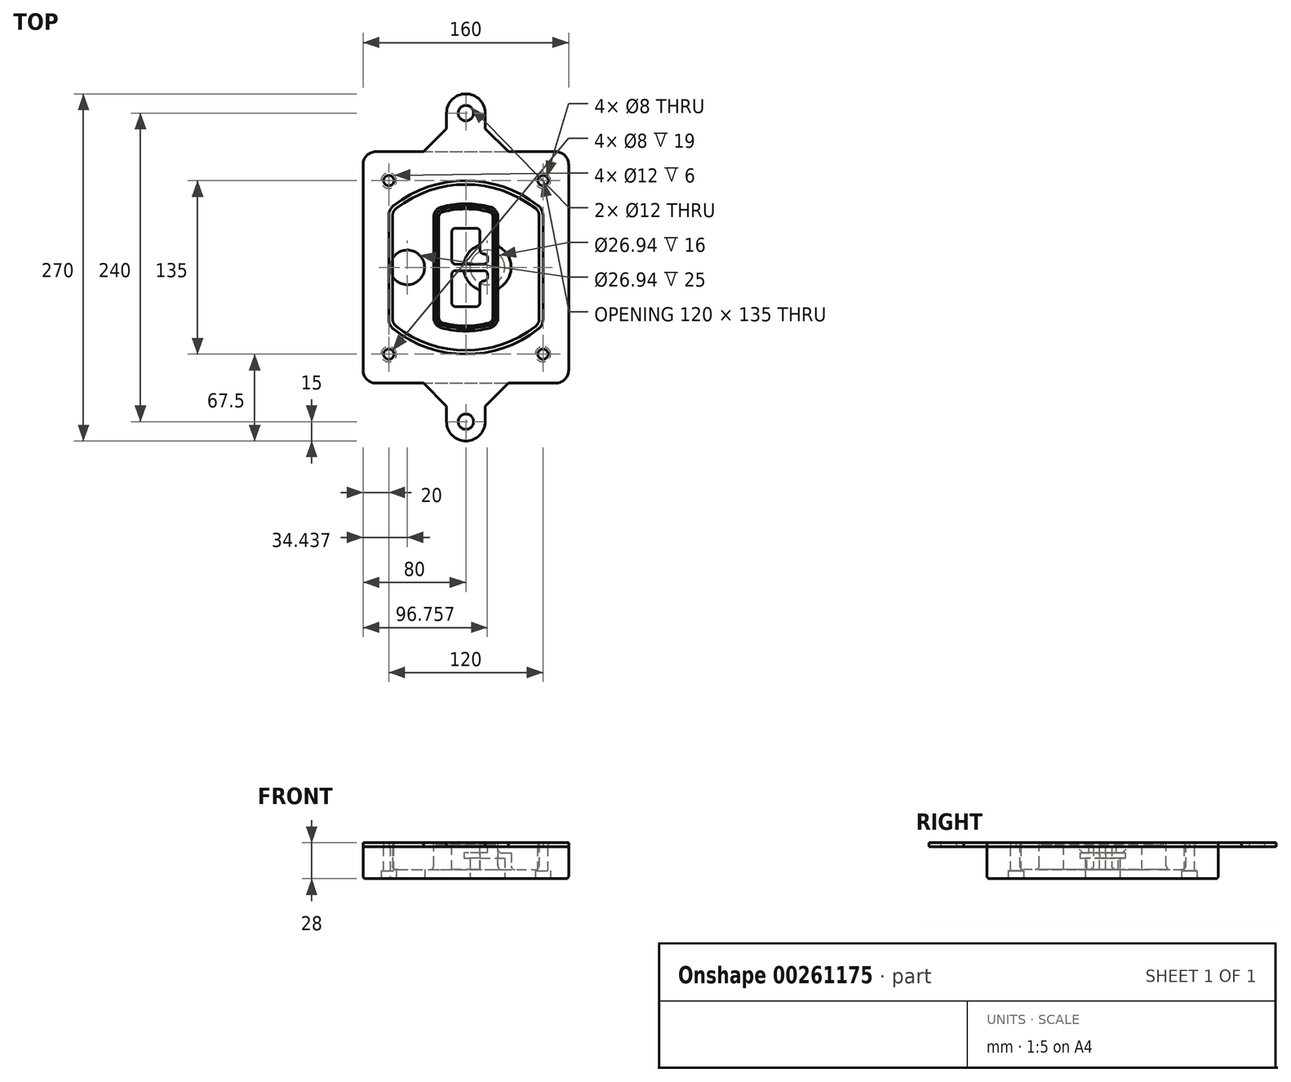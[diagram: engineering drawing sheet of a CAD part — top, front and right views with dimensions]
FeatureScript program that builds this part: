
annotation { "Feature Type Name" : "Feature", "Feature Type Description" : "" }
export const myFeature = defineFeature(function(context is Context, id is Id, definition is map)
    precondition{}
    {
        {
            var Q0;
            Q0=qCreatedBy(makeId("Top.planeOp"),FACE);
            var sketch = newSketch(context, id + "F0", { "sketchPlane" : qUnion([Q0])});
            skPoint(sketch, "E0.rect.middle", {"position": v(0, 0) * mm});
            skLineSegment(sketch, "E1.bottom", {"start": v(-70, -90) * mm, "end": v(70, -90) * mm});
            skLineSegment(sketch, "E1.top", {"start": v(-70, 90) * mm, "end": v(70, 90) * mm});
            skLineSegment(sketch, "E1.left", {"start": v(-80, -80) * mm, "end": v(-80, 80) * mm});
            skLineSegment(sketch, "E1.right", {"start": v(80, -80) * mm, "end": v(80, 80) * mm});
            skLineSegment(sketch, "E2", {"start": v(-80, 90) * mm, "end": v(80, -90) * mm, "construction": true});
            skLineSegment(sketch, "E3", {"start": v(80, 90) * mm, "end": v(-80, -90) * mm, "construction": true});
            skCircle(sketch, "E4", {"center": v(-60, 67.5) * mm, "radius": 4 * mm});
            skCircle(sketch, "E5", {"center": v(60, 67.5) * mm, "radius": 4 * mm});
            skCircle(sketch, "E6", {"center": v(60, -67.5) * mm, "radius": 4 * mm});
            skCircle(sketch, "E7", {"center": v(-60, -67.5) * mm, "radius": 4 * mm});
            skLineSegment(sketch, "E8", {"start": v(-60, 67.5) * mm, "end": v(60, 67.5) * mm, "construction": true});
            skLineSegment(sketch, "E9", {"start": v(60, 67.5) * mm, "end": v(60, -67.5) * mm, "construction": true});
            skLineSegment(sketch, "E10", {"start": v(60, -67.5) * mm, "end": v(-60, -67.5) * mm, "construction": true});
            skLineSegment(sketch, "E11", {"start": v(-60, -67.5) * mm, "end": v(-60, 67.5) * mm, "construction": true});
            skLineSegment(sketch, "E12", {"start": v(-60, 40.3) * mm, "end": v(-60, -40.3) * mm});
            skLineSegment(sketch, "E13", {"start": v(60, 40.3) * mm, "end": v(60, -40.3) * mm});
            skArc(sketch, "E14", {"start": v(56.15, 48.18) * mm, "mid": v(0, 67.5) * mm, "end": v(-56.15, 48.18) * mm});
            skArc(sketch, "E15", {"start": v(-56.15, -48.18) * mm, "mid": v(0, -67.5) * mm, "end": v(56.15, -48.18) * mm});
            skLineSegment(sketch, "E16", {"start": v(-60, 0) * mm, "end": v(60, 0) * mm, "construction": true});
            skPoint(sketch, "E17.visualSharp", {"position": v(-60, -45) * mm});
            skArc(sketch, "E17.filletArc", {"start": v(-60, -40.3) * mm, "mid": v(-58.99, -44.68) * mm, "end": v(-56.15, -48.18) * mm});
            skPoint(sketch, "E18.visualSharp", {"position": v(-60, 45) * mm});
            skArc(sketch, "E18.filletArc", {"start": v(-56.15, 48.18) * mm, "mid": v(-58.99, 44.68) * mm, "end": v(-60, 40.3) * mm});
            skPoint(sketch, "E19.visualSharp", {"position": v(60, 45) * mm});
            skArc(sketch, "E19.filletArc", {"start": v(60, 40.3) * mm, "mid": v(58.99, 44.68) * mm, "end": v(56.15, 48.18) * mm});
            skPoint(sketch, "E20.visualSharp", {"position": v(60, -45) * mm});
            skArc(sketch, "E20.filletArc", {"start": v(56.15, -48.18) * mm, "mid": v(58.99, -44.68) * mm, "end": v(60, -40.3) * mm});
            skPoint(sketch, "E21.visualSharp", {"position": v(-80, 90) * mm});
            skArc(sketch, "E21.filletArc", {"start": v(-70, 90) * mm, "mid": v(-77.07, 87.07) * mm, "end": v(-80, 80) * mm});
            skPoint(sketch, "E22.visualSharp", {"position": v(80, 90) * mm});
            skArc(sketch, "E22.filletArc", {"start": v(80, 80) * mm, "mid": v(77.07, 87.07) * mm, "end": v(70, 90) * mm});
            skPoint(sketch, "E23.visualSharp", {"position": v(80, -90) * mm});
            skArc(sketch, "E23.filletArc", {"start": v(70, -90) * mm, "mid": v(77.07, -87.07) * mm, "end": v(80, -80) * mm});
            skPoint(sketch, "E24.visualSharp", {"position": v(-80, -90) * mm});
            skArc(sketch, "E24.filletArc", {"start": v(-80, -80) * mm, "mid": v(-77.07, -87.07) * mm, "end": v(-70, -90) * mm});
            skArc(sketch, "E25.0", {"start": v(57, 40.3) * mm, "mid": v(56.3, 43.36) * mm, "end": v(54.3, 45.81) * mm});
            skLineSegment(sketch, "E25.1", {"start": v(57, 40.3) * mm, "end": v(57, -40.3) * mm});
            skArc(sketch, "E25.2", {"start": v(54.3, -45.81) * mm, "mid": v(56.3, -43.36) * mm, "end": v(57, -40.3) * mm});
            skArc(sketch, "E25.3", {"start": v(-54.3, -45.81) * mm, "mid": v(0, -64.5) * mm, "end": v(54.3, -45.81) * mm});
            skArc(sketch, "E25.4", {"start": v(-57, -40.3) * mm, "mid": v(-56.3, -43.36) * mm, "end": v(-54.3, -45.81) * mm});
            skArc(sketch, "E25.5", {"start": v(54.3, 45.81) * mm, "mid": v(0, 64.5) * mm, "end": v(-54.3, 45.81) * mm});
            skLineSegment(sketch, "E25.6", {"start": v(-57, 40.3) * mm, "end": v(-57, -40.3) * mm});
            skArc(sketch, "E25.7", {"start": v(-54.3, 45.81) * mm, "mid": v(-56.3, 43.36) * mm, "end": v(-57, 40.3) * mm});
            skArc(sketch, "E26.0", {"start": v(-58.62, 51.33) * mm, "mid": v(-62.58, 46.43) * mm, "end": v(-64, 40.3) * mm});
            skArc(sketch, "E26.1", {"start": v(58.62, 51.33) * mm, "mid": v(0, 71.5) * mm, "end": v(-58.62, 51.33) * mm});
            skArc(sketch, "E26.2", {"start": v(64, 40.3) * mm, "mid": v(62.58, 46.43) * mm, "end": v(58.62, 51.33) * mm});
            skLineSegment(sketch, "E26.3", {"start": v(64, 40.3) * mm, "end": v(64, -40.3) * mm});
            skArc(sketch, "E26.4", {"start": v(58.62, -51.33) * mm, "mid": v(62.58, -46.43) * mm, "end": v(64, -40.3) * mm});
            skLineSegment(sketch, "E26.5", {"start": v(-64, 40.3) * mm, "end": v(-64, -40.3) * mm});
            skArc(sketch, "E26.6", {"start": v(-58.62, -51.33) * mm, "mid": v(0, -71.5) * mm, "end": v(58.62, -51.33) * mm});
            skArc(sketch, "E26.7", {"start": v(-64, -40.3) * mm, "mid": v(-62.58, -46.43) * mm, "end": v(-58.62, -51.33) * mm});
            skSolve(sketch);
        }
        {
            var Q0;
            Q0=makeQuery(id+"F0.imprint","IMPRINT",FACE,{"disambiguationData":[TD([[makeQuery(id+"F0.imprint","IMPRINT",EDGE,{"derivedFrom":sQuery(id+"F0.wireOp",EDGE,"E1.bottom")}),1.0]])]});
            var Q1;
            Q1=makeQuery(id+"F0.imprint","IMPRINT",FACE,{"disambiguationData":[TD([[makeQuery(id+"F0.imprint","IMPRINT",EDGE,{"derivedFrom":sQuery(id+"F0.wireOp",EDGE,"E12")}),1.0]])]});
            var Q2;
            Q2=makeQuery(id+"F0.imprint","IMPRINT",FACE,{"disambiguationData":[TD([[makeQuery(id+"F0.imprint","IMPRINT",EDGE,{"derivedFrom":sQuery(id+"F0.wireOp",EDGE,"E25.0")}),1.0]])]});
            var Q3;
            Q3=makeQuery(id+"F0.imprint","IMPRINT",FACE,{"disambiguationData":[TD([[makeQuery(id+"F0.imprint","IMPRINT",EDGE,{"derivedFrom":sQuery(id+"F0.wireOp",EDGE,"E12")}),-1.0]])]});
            extrude(context, id + "F1", {"entities" : qUnion([Q0, Q1, Q2, Q3]), "oppositeDirection" : true, "depth" : 25 * mm});
        }
        {
            var Q0;
            Q0=makeQuery(id+"F0.imprint","IMPRINT",FACE,{"disambiguationData":[TD([[makeQuery(id+"F0.imprint","IMPRINT",EDGE,{"derivedFrom":sQuery(id+"F0.wireOp",EDGE,"E12")}),1.0]])]});
            extrude(context, id + "F2", {"entities" : qUnion([Q0]), "operationType" : NewBodyOperationType.ADD, "depth" : 3 * mm});
        }
        {
            var Q0;
            Q0=makeQuery(id+"F0.imprint","IMPRINT",FACE,{"disambiguationData":[TD([[makeQuery(id+"F0.imprint","IMPRINT",EDGE,{"derivedFrom":sQuery(id+"F0.wireOp",EDGE,"E25.0")}),1.0]])]});
            extrude(context, id + "F3", {"entities" : qUnion([Q0]), "operationType" : NewBodyOperationType.REMOVE, "oppositeDirection" : true, "depth" : 18 * mm});
        }
        {
            var Q0;
            Q0=makeQuery(id+"F2.opExtrude","CAP_FACE",FACE,{"disambiguationData":[OSD([sQuery(id+"F0.wireOp",EDGE,"E12"),sQuery(id+"F0.wireOp",EDGE,"E13"),sQuery(id+"F0.wireOp",EDGE,"E14"),sQuery(id+"F0.wireOp",EDGE,"E15"),sQuery(id+"F0.wireOp",EDGE,"E17.filletArc"),sQuery(id+"F0.wireOp",EDGE,"E18.filletArc"),sQuery(id+"F0.wireOp",EDGE,"E19.filletArc"),sQuery(id+"F0.wireOp",EDGE,"E20.filletArc"),sQuery(id+"F0.wireOp",EDGE,"E25.0"),sQuery(id+"F0.wireOp",EDGE,"E25.1"),sQuery(id+"F0.wireOp",EDGE,"E25.2"),sQuery(id+"F0.wireOp",EDGE,"E25.3"),sQuery(id+"F0.wireOp",EDGE,"E25.4"),sQuery(id+"F0.wireOp",EDGE,"E25.5"),sQuery(id+"F0.wireOp",EDGE,"E25.6"),sQuery(id+"F0.wireOp",EDGE,"E25.7")])],"isStart":false});
            var sketch = newSketch(context, id + "F4", { "sketchPlane" : qUnion([Q0])});
            skArc(sketch, "E27.0", {"start": v(-19.08, -46.97) * mm, "mid": v(0, -49.5) * mm, "end": v(19.08, -46.97) * mm});
            skArc(sketch, "E28.0", {"start": v(19.08, 46.97) * mm, "mid": v(0, 49.5) * mm, "end": v(-19.08, 46.97) * mm});
            skLineSegment(sketch, "E29", {"start": v(-25, 39.25) * mm, "end": v(-25, -39.25) * mm});
            skLineSegment(sketch, "E30", {"start": v(25, 39.25) * mm, "end": v(25, -39.25) * mm});
            skLineSegment(sketch, "E31", {"start": v(-25, 45.1) * mm, "end": v(25, 45.1) * mm, "construction": true});
            skLineSegment(sketch, "E32", {"start": v(-25, -45.1) * mm, "end": v(25, -45.1) * mm, "construction": true});
            skPoint(sketch, "E33.visualSharp", {"position": v(-25, 45.1) * mm});
            skArc(sketch, "E33.filletArc", {"start": v(-19.08, 46.97) * mm, "mid": v(-23.35, 44.11) * mm, "end": v(-25, 39.25) * mm});
            skPoint(sketch, "E34.visualSharp", {"position": v(25, 45.1) * mm});
            skArc(sketch, "E34.filletArc", {"start": v(25, 39.25) * mm, "mid": v(23.35, 44.11) * mm, "end": v(19.08, 46.97) * mm});
            skPoint(sketch, "E35.visualSharp", {"position": v(25, -45.1) * mm});
            skArc(sketch, "E35.filletArc", {"start": v(19.08, -46.97) * mm, "mid": v(23.35, -44.11) * mm, "end": v(25, -39.25) * mm});
            skPoint(sketch, "E36.visualSharp", {"position": v(-25, -45.1) * mm});
            skArc(sketch, "E36.filletArc", {"start": v(-25, -39.25) * mm, "mid": v(-23.35, -44.11) * mm, "end": v(-19.08, -46.97) * mm});
            skArc(sketch, "E37.0", {"start": v(54.3, 45.81) * mm, "mid": v(0, 64.5) * mm, "end": v(-54.3, 45.81) * mm});
            skArc(sketch, "E37.1", {"start": v(-54.3, 45.81) * mm, "mid": v(-56.3, 43.36) * mm, "end": v(-57, 40.3) * mm});
            skLineSegment(sketch, "E37.2", {"start": v(-57, 40.3) * mm, "end": v(-57, -40.3) * mm});
            skArc(sketch, "E37.3", {"start": v(-57, -40.3) * mm, "mid": v(-56.3, -43.36) * mm, "end": v(-54.3, -45.81) * mm});
            skArc(sketch, "E37.4", {"start": v(-54.3, -45.81) * mm, "mid": v(0, -64.5) * mm, "end": v(54.3, -45.81) * mm});
            skArc(sketch, "E37.5", {"start": v(54.3, -45.81) * mm, "mid": v(56.3, -43.36) * mm, "end": v(57, -40.3) * mm});
            skLineSegment(sketch, "E37.6", {"start": v(57, 40.3) * mm, "end": v(57, -40.3) * mm});
            skArc(sketch, "E37.7", {"start": v(57, 40.3) * mm, "mid": v(56.3, 43.36) * mm, "end": v(54.3, 45.81) * mm});
            skLineSegment(sketch, "E38.0", {"start": v(23, 39.25) * mm, "end": v(23, -39.25) * mm});
            skArc(sketch, "E38.1", {"start": v(18.56, -45.04) * mm, "mid": v(21.76, -42.9) * mm, "end": v(23, -39.25) * mm});
            skArc(sketch, "E38.2", {"start": v(-18.56, -45.04) * mm, "mid": v(0, -47.5) * mm, "end": v(18.56, -45.04) * mm});
            skArc(sketch, "E38.3", {"start": v(-23, -39.25) * mm, "mid": v(-21.76, -42.9) * mm, "end": v(-18.56, -45.04) * mm});
            skLineSegment(sketch, "E38.4", {"start": v(-23, 39.25) * mm, "end": v(-23, -39.25) * mm});
            skArc(sketch, "E38.5", {"start": v(23, 39.25) * mm, "mid": v(21.76, 42.9) * mm, "end": v(18.56, 45.04) * mm});
            skArc(sketch, "E38.6", {"start": v(-18.56, 45.04) * mm, "mid": v(-21.76, 42.9) * mm, "end": v(-23, 39.25) * mm});
            skArc(sketch, "E38.7", {"start": v(18.56, 45.04) * mm, "mid": v(0, 47.5) * mm, "end": v(-18.56, 45.04) * mm});
            skArc(sketch, "E39.0", {"start": v(21, 39.25) * mm, "mid": v(20.18, 41.68) * mm, "end": v(18.04, 43.1) * mm});
            skLineSegment(sketch, "E39.1", {"start": v(21, 39.25) * mm, "end": v(21, -39.25) * mm});
            skArc(sketch, "E39.2", {"start": v(18.04, -43.1) * mm, "mid": v(20.18, -41.68) * mm, "end": v(21, -39.25) * mm});
            skArc(sketch, "E39.3", {"start": v(-18.04, -43.1) * mm, "mid": v(0, -45.5) * mm, "end": v(18.04, -43.1) * mm});
            skArc(sketch, "E39.4", {"start": v(-21, -39.25) * mm, "mid": v(-20.18, -41.68) * mm, "end": v(-18.04, -43.1) * mm});
            skArc(sketch, "E39.5", {"start": v(18.04, 43.1) * mm, "mid": v(0, 45.5) * mm, "end": v(-18.04, 43.1) * mm});
            skLineSegment(sketch, "E39.6", {"start": v(-21, 39.25) * mm, "end": v(-21, -39.25) * mm});
            skArc(sketch, "E39.7", {"start": v(-18.04, 43.1) * mm, "mid": v(-20.18, 41.68) * mm, "end": v(-21, 39.25) * mm});
            skLineSegment(sketch, "E40", {"start": v(-25, 0) * mm, "end": v(25, 0) * mm, "construction": true});
            skLineSegment(sketch, "E41", {"start": v(-11, 5.5) * mm, "end": v(-11, 27.5) * mm});
            skLineSegment(sketch, "E42", {"start": v(-8, 30.5) * mm, "end": v(8, 30.5) * mm});
            skLineSegment(sketch, "E43", {"start": v(11, 27.5) * mm, "end": v(11, 13.5) * mm});
            skLineSegment(sketch, "E44", {"start": v(14, 10.5) * mm, "end": v(14, 10.5) * mm});
            skLineSegment(sketch, "E45", {"start": v(17, 7.5) * mm, "end": v(17, 5.5) * mm});
            skLineSegment(sketch, "E46", {"start": v(14, 2.5) * mm, "end": v(-8, 2.5) * mm});
            skPoint(sketch, "E47.visualSharp", {"position": v(-11, 30.5) * mm});
            skArc(sketch, "E47.filletArc", {"start": v(-8, 30.5) * mm, "mid": v(-10.12, 29.62) * mm, "end": v(-11, 27.5) * mm});
            skPoint(sketch, "E48.visualSharp", {"position": v(11, 30.5) * mm});
            skArc(sketch, "E48.filletArc", {"start": v(11, 27.5) * mm, "mid": v(10.12, 29.62) * mm, "end": v(8, 30.5) * mm});
            skPoint(sketch, "E49.visualSharp", {"position": v(11, 10.5) * mm});
            skArc(sketch, "E49.filletArc", {"start": v(11, 13.5) * mm, "mid": v(11.88, 11.38) * mm, "end": v(14, 10.5) * mm});
            skPoint(sketch, "E50.visualSharp", {"position": v(17, 10.5) * mm});
            skArc(sketch, "E50.filletArc", {"start": v(17, 7.5) * mm, "mid": v(16.12, 9.62) * mm, "end": v(14, 10.5) * mm});
            skPoint(sketch, "E51.visualSharp", {"position": v(17, 2.5) * mm});
            skArc(sketch, "E51.filletArc", {"start": v(14, 2.5) * mm, "mid": v(16.12, 3.38) * mm, "end": v(17, 5.5) * mm});
            skPoint(sketch, "E52.visualSharp", {"position": v(-11, 2.5) * mm});
            skArc(sketch, "E52.filletArc", {"start": v(-11, 5.5) * mm, "mid": v(-10.12, 3.38) * mm, "end": v(-8, 2.5) * mm});
            skLineSegment(sketch, "E53.0.MirrorCS", {"start": v(14, -2.5) * mm, "end": v(-8, -2.5) * mm});
            skArc(sketch, "E54.0.MirrorCS", {"start": v(-11, -5.5) * mm, "mid": v(-10.12, -3.38) * mm, "end": v(-8, -2.5) * mm});
            skLineSegment(sketch, "E55.0.MirrorCS", {"start": v(-11, -5.5) * mm, "end": v(-11, -27.5) * mm});
            skArc(sketch, "E56.0.MirrorCS", {"start": v(-8, -30.5) * mm, "mid": v(-10.12, -29.62) * mm, "end": v(-11, -27.5) * mm});
            skLineSegment(sketch, "E57.0.MirrorCS", {"start": v(-8, -30.5) * mm, "end": v(8, -30.5) * mm});
            skArc(sketch, "E58.0.MirrorCS", {"start": v(11, -27.5) * mm, "mid": v(10.12, -29.62) * mm, "end": v(8, -30.5) * mm});
            skLineSegment(sketch, "E59.0.MirrorCS", {"start": v(11, -27.5) * mm, "end": v(11, -13.5) * mm});
            skArc(sketch, "E60.0.MirrorCS", {"start": v(11, -13.5) * mm, "mid": v(11.88, -11.38) * mm, "end": v(14, -10.5) * mm});
            skArc(sketch, "E61.0.MirrorCS", {"start": v(17, -7.5) * mm, "mid": v(16.12, -9.62) * mm, "end": v(14, -10.5) * mm});
            skLineSegment(sketch, "E62.0.MirrorCS", {"start": v(17, -7.5) * mm, "end": v(17, -5.5) * mm});
            skArc(sketch, "E63.0.MirrorCS", {"start": v(14, -2.5) * mm, "mid": v(16.12, -3.38) * mm, "end": v(17, -5.5) * mm});
            skSolve(sketch);
        }
        {
            var Q0;
            Q0=makeQuery(id+"F4.imprint","IMPRINT",FACE,{"disambiguationData":[TD([[makeQuery(id+"F4.imprint","IMPRINT",EDGE,{"derivedFrom":sQuery(id+"F4.wireOp",EDGE,"E27.0")}),1.0]])]});
            var Q1;
            Q1=makeQuery(id+"F4.imprint","IMPRINT",FACE,{"disambiguationData":[TD([[makeQuery(id+"F4.imprint","IMPRINT",EDGE,{"derivedFrom":sQuery(id+"F4.wireOp",EDGE,"E38.0")}),-1.0]])]});
            var Q2;
            Q2=makeQuery(id+"F4.imprint","IMPRINT",FACE,{"disambiguationData":[TD([[makeQuery(id+"F4.imprint","IMPRINT",EDGE,{"derivedFrom":sQuery(id+"F4.wireOp",EDGE,"E39.0")}),1.0]])]});
            extrude(context, id + "F5", {"entities" : qUnion([Q0, Q1, Q2]), "operationType" : NewBodyOperationType.ADD, "endBound" : BoundingType.UP_TO_NEXT, "oppositeDirection" : true, "depth" : 25 * mm});
        }
        {
            var Q0;
            Q0=makeQuery(id+"F4.imprint","IMPRINT",FACE,{"disambiguationData":[TD([[makeQuery(id+"F4.imprint","IMPRINT",EDGE,{"derivedFrom":sQuery(id+"F4.wireOp",EDGE,"E38.0")}),-1.0]])]});
            extrude(context, id + "F6", {"entities" : qUnion([Q0]), "operationType" : NewBodyOperationType.REMOVE, "oppositeDirection" : true, "depth" : 2 * mm});
        }
        {
            var Q0;
            Q0=makeQuery(id+"F1.opExtrude","CAP_FACE",FACE,{"disambiguationData":[OSD([sQuery(id+"F0.wireOp",EDGE,"E1.bottom"),sQuery(id+"F0.wireOp",EDGE,"E1.top"),sQuery(id+"F0.wireOp",EDGE,"E1.left"),sQuery(id+"F0.wireOp",EDGE,"E1.right"),sQuery(id+"F0.wireOp",EDGE,"E4"),sQuery(id+"F0.wireOp",EDGE,"E5"),sQuery(id+"F0.wireOp",EDGE,"E6"),sQuery(id+"F0.wireOp",EDGE,"E7"),sQuery(id+"F0.wireOp",EDGE,"E21.filletArc"),sQuery(id+"F0.wireOp",EDGE,"E22.filletArc"),sQuery(id+"F0.wireOp",EDGE,"E23.filletArc"),sQuery(id+"F0.wireOp",EDGE,"E24.filletArc")])],"isStart":false});
            var sketch = newSketch(context, id + "F7", { "sketchPlane" : qUnion([Q0])});
            skCircle(sketch, "E64", {"center": v(16.76, 0) * mm, "radius": 13.47 * mm});
            skCircle(sketch, "E65", {"center": v(-45.56, 0) * mm, "radius": 13.47 * mm});
            skLineSegment(sketch, "E66", {"start": v(80, 0) * mm, "end": v(-80, 0) * mm});
            skCircle(sketch, "E67", {"center": v(16.76, 0) * mm, "radius": 18.47 * mm});
            skCircle(sketch, "E68", {"center": v(60, -67.5) * mm, "radius": 6 * mm});
            skCircle(sketch, "E69", {"center": v(-60, -67.5) * mm, "radius": 6 * mm});
            skCircle(sketch, "E70", {"center": v(-60, 67.5) * mm, "radius": 6 * mm});
            skCircle(sketch, "E71", {"center": v(60, 67.5) * mm, "radius": 6 * mm});
            skSolve(sketch);
        }
        {
            var Q0;
            {var subQ1=sQuery(id+"F7.wireOp",EDGE,"E66");var subQ4=sQuery(id+"F7.wireOp",EDGE,"E64");var subQ6=makeQuery(id+"F7.imprint","INTERSECT",VERTEX,{"disambiguationData":[OD(0.0)],"derivedFrom":[subQ4,subQ1]});Q0=makeQuery(id+"F7.imprint","IMPRINT",FACE,{"disambiguationData":[TD([[makeQuery(id+"F7.imprint","IMPRINT",EDGE,{"disambiguationData":[TD([[subQ6,-1.0]])],"derivedFrom":subQ4}),-1.0]])]});}
            var Q1;
            {var subQ0=sQuery(id+"F7.wireOp",EDGE,"E66");var subQ1=sQuery(id+"F7.wireOp",EDGE,"E64");var subQ3=makeQuery(id+"F7.imprint","INTERSECT",VERTEX,{"disambiguationData":[OD(0.0)],"derivedFrom":[subQ1,subQ0]});Q1=makeQuery(id+"F7.imprint","IMPRINT",FACE,{"disambiguationData":[TD([[makeQuery(id+"F7.imprint","IMPRINT",EDGE,{"disambiguationData":[TD([[subQ3,-1.0]])],"derivedFrom":subQ1}),1.0]])]});}
            var Q2;
            {var subQ0=sQuery(id+"F7.wireOp",EDGE,"E66");var subQ1=sQuery(id+"F7.wireOp",EDGE,"E64");var subQ3=makeQuery(id+"F7.imprint","INTERSECT",VERTEX,{"disambiguationData":[OD(0.0)],"derivedFrom":[subQ1,subQ0]});Q2=makeQuery(id+"F7.imprint","IMPRINT",FACE,{"disambiguationData":[TD([[makeQuery(id+"F7.imprint","IMPRINT",EDGE,{"disambiguationData":[TD([[subQ3,1.0]])],"derivedFrom":subQ1}),1.0]])]});}
            var Q3;
            {var subQ1=sQuery(id+"F7.wireOp",EDGE,"E66");var subQ4=sQuery(id+"F7.wireOp",EDGE,"E64");var subQ6=makeQuery(id+"F7.imprint","INTERSECT",VERTEX,{"disambiguationData":[OD(0.0)],"derivedFrom":[subQ4,subQ1]});Q3=makeQuery(id+"F7.imprint","IMPRINT",FACE,{"disambiguationData":[TD([[makeQuery(id+"F7.imprint","IMPRINT",EDGE,{"disambiguationData":[TD([[subQ6,1.0]])],"derivedFrom":subQ4}),-1.0]])]});}
            extrude(context, id + "F8", {"entities" : qUnion([Q0, Q1, Q2, Q3]), "operationType" : NewBodyOperationType.ADD, "oppositeDirection" : true, "depth" : 20 * mm});
        }
        {
            var Q0;
            {var subQ0=sQuery(id+"F7.wireOp",EDGE,"E66");var subQ1=sQuery(id+"F7.wireOp",EDGE,"E64");var subQ3=makeQuery(id+"F7.imprint","INTERSECT",VERTEX,{"disambiguationData":[OD(0.0)],"derivedFrom":[subQ1,subQ0]});Q0=makeQuery(id+"F7.imprint","IMPRINT",FACE,{"disambiguationData":[TD([[makeQuery(id+"F7.imprint","IMPRINT",EDGE,{"disambiguationData":[TD([[subQ3,-1.0]])],"derivedFrom":subQ1}),1.0]])]});}
            var Q1;
            {var subQ0=sQuery(id+"F7.wireOp",EDGE,"E66");var subQ1=sQuery(id+"F7.wireOp",EDGE,"E64");var subQ3=makeQuery(id+"F7.imprint","INTERSECT",VERTEX,{"disambiguationData":[OD(0.0)],"derivedFrom":[subQ1,subQ0]});Q1=makeQuery(id+"F7.imprint","IMPRINT",FACE,{"disambiguationData":[TD([[makeQuery(id+"F7.imprint","IMPRINT",EDGE,{"disambiguationData":[TD([[subQ3,1.0]])],"derivedFrom":subQ1}),1.0]])]});}
            extrude(context, id + "F9", {"entities" : qUnion([Q0, Q1]), "operationType" : NewBodyOperationType.REMOVE, "oppositeDirection" : true, "depth" : 16 * mm});
        }
        {
            var Q0;
            {var subQ0=sQuery(id+"F7.wireOp",EDGE,"E66");var subQ1=sQuery(id+"F7.wireOp",EDGE,"E65");var subQ3=makeQuery(id+"F7.imprint","INTERSECT",VERTEX,{"disambiguationData":[OD(0.0)],"derivedFrom":[subQ1,subQ0]});Q0=makeQuery(id+"F7.imprint","IMPRINT",FACE,{"disambiguationData":[TD([[makeQuery(id+"F7.imprint","IMPRINT",EDGE,{"disambiguationData":[TD([[subQ3,-1.0]])],"derivedFrom":subQ1}),1.0]])]});}
            var Q1;
            {var subQ0=sQuery(id+"F7.wireOp",EDGE,"E66");var subQ1=sQuery(id+"F7.wireOp",EDGE,"E65");var subQ3=makeQuery(id+"F7.imprint","INTERSECT",VERTEX,{"disambiguationData":[OD(0.0)],"derivedFrom":[subQ1,subQ0]});Q1=makeQuery(id+"F7.imprint","IMPRINT",FACE,{"disambiguationData":[TD([[makeQuery(id+"F7.imprint","IMPRINT",EDGE,{"disambiguationData":[TD([[subQ3,1.0]])],"derivedFrom":subQ1}),1.0]])]});}
            extrude(context, id + "F10", {"entities" : qUnion([Q0, Q1]), "operationType" : NewBodyOperationType.REMOVE, "oppositeDirection" : true, "depth" : 25 * mm});
        }
        {
            var Q0;
            Q0=makeQuery(id+"F7.imprint","IMPRINT",FACE,{"disambiguationData":[TD([[makeQuery(id+"F7.imprint","IMPRINT",EDGE,{"derivedFrom":sQuery(id+"F7.wireOp",EDGE,"E68")}),1.0]])]});
            var Q1;
            Q1=makeQuery(id+"F7.imprint","IMPRINT",FACE,{"disambiguationData":[TD([[makeQuery(id+"F7.imprint","IMPRINT",EDGE,{"derivedFrom":makeQuery(id+"F1.opExtrude","CAP_EDGE",EDGE,{"disambiguationData":[OSD([sQuery(id+"F0.wireOp",EDGE,"E5")])],"isStart":false})}),-1.0]])]});
            var Q2;
            Q2=makeQuery(id+"F7.imprint","IMPRINT",FACE,{"disambiguationData":[TD([[makeQuery(id+"F7.imprint","IMPRINT",EDGE,{"derivedFrom":sQuery(id+"F7.wireOp",EDGE,"E69")}),1.0]])]});
            var Q3;
            Q3=makeQuery(id+"F7.imprint","IMPRINT",FACE,{"disambiguationData":[TD([[makeQuery(id+"F7.imprint","IMPRINT",EDGE,{"derivedFrom":makeQuery(id+"F1.opExtrude","CAP_EDGE",EDGE,{"disambiguationData":[OSD([sQuery(id+"F0.wireOp",EDGE,"E4")])],"isStart":false})}),-1.0]])]});
            var Q4;
            Q4=makeQuery(id+"F7.imprint","IMPRINT",FACE,{"disambiguationData":[TD([[makeQuery(id+"F7.imprint","IMPRINT",EDGE,{"derivedFrom":sQuery(id+"F7.wireOp",EDGE,"E70")}),1.0]])]});
            var Q5;
            Q5=makeQuery(id+"F7.imprint","IMPRINT",FACE,{"disambiguationData":[TD([[makeQuery(id+"F7.imprint","IMPRINT",EDGE,{"derivedFrom":makeQuery(id+"F1.opExtrude","CAP_EDGE",EDGE,{"disambiguationData":[OSD([sQuery(id+"F0.wireOp",EDGE,"E7")])],"isStart":false})}),-1.0]])]});
            var Q6;
            Q6=makeQuery(id+"F7.imprint","IMPRINT",FACE,{"disambiguationData":[TD([[makeQuery(id+"F7.imprint","IMPRINT",EDGE,{"derivedFrom":sQuery(id+"F7.wireOp",EDGE,"E71")}),1.0]])]});
            var Q7;
            Q7=makeQuery(id+"F7.imprint","IMPRINT",FACE,{"disambiguationData":[TD([[makeQuery(id+"F7.imprint","IMPRINT",EDGE,{"derivedFrom":makeQuery(id+"F1.opExtrude","CAP_EDGE",EDGE,{"disambiguationData":[OSD([sQuery(id+"F0.wireOp",EDGE,"E6")])],"isStart":false})}),-1.0]])]});
            extrude(context, id + "F11", {"entities" : qUnion([Q0, Q1, Q2, Q3, Q4, Q5, Q6, Q7]), "operationType" : NewBodyOperationType.REMOVE, "oppositeDirection" : true, "depth" : 6 * mm});
        }
        {
            var Q0;
            Q0=makeQuery(id+"F9.boolean.opBoolean","COPY",FACE,{"derivedFrom":makeQuery(id+"F9.opExtrude","CAP_FACE",FACE,{"disambiguationData":[OSD([sQuery(id+"F7.wireOp",EDGE,"E64")])],"isStart":false})});
            var sketch = newSketch(context, id + "F12", { "sketchPlane" : qUnion([Q0])});
            skArc(sketch, "E72.0", {"start": v(11, 17.55) * mm, "mid": v(2.57, 11.82) * mm, "end": v(-1.54, 2.5) * mm});
            skArc(sketch, "E72.1", {"start": v(-1.54, -2.5) * mm, "mid": v(2.57, -11.82) * mm, "end": v(11, -17.55) * mm});
            skLineSegment(sketch, "E73", {"start": v(-1.54, -2.5) * mm, "end": v(14, -2.5) * mm});
            skLineSegment(sketch, "E74.0", {"start": v(14, 2.5) * mm, "end": v(-1.54, 2.5) * mm});
            skArc(sketch, "E74.1", {"start": v(14, 2.5) * mm, "mid": v(16.12, 3.38) * mm, "end": v(17, 5.5) * mm});
            skLineSegment(sketch, "E74.2", {"start": v(17, 7.5) * mm, "end": v(17, 5.5) * mm});
            skArc(sketch, "E74.3", {"start": v(17, 7.5) * mm, "mid": v(16.12, 9.62) * mm, "end": v(14, 10.5) * mm});
            skArc(sketch, "E74.4", {"start": v(11, 13.5) * mm, "mid": v(11.88, 11.38) * mm, "end": v(14, 10.5) * mm});
            skLineSegment(sketch, "E74.5", {"start": v(11, 17.55) * mm, "end": v(11, 13.5) * mm});
            skLineSegment(sketch, "E74.7", {"start": v(14, -2.5) * mm, "end": v(-1.54, -2.5) * mm});
            skArc(sketch, "E74.8", {"start": v(14, -2.5) * mm, "mid": v(16.12, -3.38) * mm, "end": v(17, -5.5) * mm});
            skLineSegment(sketch, "E74.9", {"start": v(17, -7.5) * mm, "end": v(17, -5.5) * mm});
            skArc(sketch, "E74.10", {"start": v(17, -7.5) * mm, "mid": v(16.12, -9.62) * mm, "end": v(14, -10.5) * mm});
            skArc(sketch, "E74.11", {"start": v(11, -13.5) * mm, "mid": v(11.88, -11.38) * mm, "end": v(14, -10.5) * mm});
            skLineSegment(sketch, "E74.12", {"start": v(11, -17.55) * mm, "end": v(11, -13.5) * mm});
            skPoint(sketch, "E75.orphan", {"position": v(11, -27.5) * mm});
            skPoint(sketch, "E76.orphan", {"position": v(-8, -2.5) * mm});
            skPoint(sketch, "E77.orphan", {"position": v(-8, 2.5) * mm});
            skPoint(sketch, "E78.orphan", {"position": v(11, 27.5) * mm});
            skSolve(sketch);
        }
        {
            var Q0;
            {var subQ7=sQuery(id+"F12.wireOp",EDGE,"E72.0");var subQ14=sQuery(id+"F12.wireOp",EDGE,"E72.1");var subQ16=sQuery(id+"F12.wireOp",EDGE,"E74.1");var subQ18=sQuery(id+"F12.wireOp",EDGE,"E74.8");Q0=qUnion([makeQuery(id+"F12.imprint","IMPRINT",FACE,{"disambiguationData":[TD([[makeQuery(id+"F12.imprint","IMPRINT",EDGE,{"derivedFrom":subQ7}),1.0]])]}),makeQuery(id+"F12.imprint","IMPRINT",FACE,{"disambiguationData":[TD([[makeQuery(id+"F12.imprint","IMPRINT",EDGE,{"derivedFrom":subQ14}),1.0]])]}),makeQuery(id+"F12.imprint","IMPRINT",FACE,{"disambiguationData":[TD([[makeQuery(id+"F12.imprint","IMPRINT",EDGE,{"derivedFrom":subQ16}),1.0]])]}),makeQuery(id+"F12.imprint","IMPRINT",FACE,{"disambiguationData":[TD([[makeQuery(id+"F12.imprint","IMPRINT",EDGE,{"derivedFrom":subQ18}),-1.0]])]})]);}
            var Q1;
            Q1=makeQuery(id+"F5.boolean.opBoolean","SPLIT",FACE,{"disambiguationData":[TD([makeQuery(id+"F5.opExtrude","SWEPT_FACE",FACE,{"disambiguationData":[OSD([sQuery(id+"F4.wireOp",EDGE,"E41")])]})])],"derivedFrom":makeQuery(id+"F3.boolean.opBoolean","COPY",FACE,{"derivedFrom":makeQuery(id+"F3.opExtrude","CAP_FACE",FACE,{"disambiguationData":[OSD([sQuery(id+"F0.wireOp",EDGE,"E25.0"),sQuery(id+"F0.wireOp",EDGE,"E25.1"),sQuery(id+"F0.wireOp",EDGE,"E25.2"),sQuery(id+"F0.wireOp",EDGE,"E25.3"),sQuery(id+"F0.wireOp",EDGE,"E25.4"),sQuery(id+"F0.wireOp",EDGE,"E25.5"),sQuery(id+"F0.wireOp",EDGE,"E25.6"),sQuery(id+"F0.wireOp",EDGE,"E25.7")])],"isStart":false})})});
            extrude(context, id + "F13", {"entities" : qUnion([Q0]), "operationType" : NewBodyOperationType.REMOVE, "endBound" : BoundingType.UP_TO_SURFACE, "endBoundEntityFace" : qUnion([Q1]), "depth" : 25 * mm});
        }
        {
            var Q0;
            Q0=makeQuery(id+"F3.boolean.opBoolean","COPY",EDGE,{"derivedFrom":makeQuery(id+"F3.opExtrude","CAP_EDGE",EDGE,{"disambiguationData":[OSD([sQuery(id+"F0.wireOp",EDGE,"E25.6")])],"isStart":false})});
            var Q1;
            Q1=makeQuery(id+"F8.boolean.opBoolean","INTERSECT",EDGE,{"derivedFrom":[makeQuery(id+"F5.opExtrude","SWEPT_FACE",FACE,{"disambiguationData":[OSD([sQuery(id+"F4.wireOp",EDGE,"E30")])]}),makeQuery(id+"F8.opExtrude","CAP_FACE",FACE,{"disambiguationData":[OSD([sQuery(id+"F7.wireOp",EDGE,"E67")])],"isStart":false})]});
            var Q2;
            Q2=makeQuery(id+"F8.boolean.opBoolean","INTERSECT",EDGE,{"disambiguationData":[OD(1.0)],"derivedFrom":[makeQuery(id+"F5.opExtrude","SWEPT_FACE",FACE,{"disambiguationData":[OSD([sQuery(id+"F4.wireOp",EDGE,"E30")])]}),makeQuery(id+"F8.opExtrude","SWEPT_FACE",FACE,{"disambiguationData":[OSD([sQuery(id+"F7.wireOp",EDGE,"E67")])]})]});
            var Q3;
            {var subQ0=sQuery(id+"F4.wireOp",EDGE,"E30");Q3=makeQuery(id+"F8.boolean.opBoolean","SPLIT",EDGE,{"disambiguationData":[TD([makeQuery(id+"F5.opExtrude","SWEPT_FACE",FACE,{"disambiguationData":[OSD([sQuery(id+"F4.wireOp",EDGE,"E35.filletArc")])]})])],"derivedFrom":makeQuery(id+"F5.opExtrude","CAP_EDGE",EDGE,{"disambiguationData":[OSD([subQ0])],"isStart":false})});}
            var Q4;
            {var subQ0=sQuery(id+"F0.wireOp",EDGE,"E25.7");var subQ1=sQuery(id+"F0.wireOp",EDGE,"E25.1");var subQ2=sQuery(id+"F0.wireOp",EDGE,"E25.6");var subQ3=sQuery(id+"F0.wireOp",EDGE,"E25.5");var subQ4=sQuery(id+"F0.wireOp",EDGE,"E25.4");var subQ5=sQuery(id+"F0.wireOp",EDGE,"E25.0");var subQ6=sQuery(id+"F0.wireOp",EDGE,"E25.2");var subQ7=sQuery(id+"F0.wireOp",EDGE,"E25.3");Q4=makeQuery(id+"F8.boolean.opBoolean","INTERSECT",EDGE,{"derivedFrom":[makeQuery(id+"F5.boolean.opBoolean","SPLIT",FACE,{"disambiguationData":[TD([makeQuery(id+"F2.opExtrude","SWEPT_FACE",FACE,{"disambiguationData":[OSD([subQ5])]})])],"derivedFrom":makeQuery(id+"F3.boolean.opBoolean","COPY",FACE,{"derivedFrom":makeQuery(id+"F3.opExtrude","CAP_FACE",FACE,{"disambiguationData":[OSD([subQ5,subQ1,subQ6,subQ7,subQ4,subQ3,subQ2,subQ0])],"isStart":false})})}),makeQuery(id+"F8.opExtrude","SWEPT_FACE",FACE,{"disambiguationData":[OSD([sQuery(id+"F7.wireOp",EDGE,"E67")])]})]});}
            var Q5;
            Q5=makeQuery(id+"F8.boolean.opBoolean","INTERSECT",EDGE,{"disambiguationData":[OD(0.0)],"derivedFrom":[makeQuery(id+"F5.opExtrude","SWEPT_FACE",FACE,{"disambiguationData":[OSD([sQuery(id+"F4.wireOp",EDGE,"E30")])]}),makeQuery(id+"F8.opExtrude","SWEPT_FACE",FACE,{"disambiguationData":[OSD([sQuery(id+"F7.wireOp",EDGE,"E67")])]})]});
            fillet(context, id + "F14", {"entities" : qUnion([Q0, Q1, Q2, Q3, Q4, Q5]), "radius" : 3 * mm, "tangentPropagation" : true, "allowEdgeOverflow" : false});
        }
        {
            var Q0;
            Q0=makeQuery(id+"F1.opExtrude","CAP_EDGE",EDGE,{"disambiguationData":[OSD([sQuery(id+"F0.wireOp",EDGE,"E1.bottom")])],"isStart":false});
            fillet(context, id + "F15", {"entities" : qUnion([Q0]), "radius" : 2 * mm, "tangentPropagation" : true, "allowEdgeOverflow" : false});
        }
        {
            var Q0;
            {var subQ0=sQuery(id+"F0.wireOp",EDGE,"E22.filletArc");var subQ1=sQuery(id+"F0.wireOp",EDGE,"E7");var subQ2=sQuery(id+"F0.wireOp",EDGE,"E6");var subQ3=sQuery(id+"F0.wireOp",EDGE,"E5");var subQ4=sQuery(id+"F0.wireOp",EDGE,"E4");var subQ5=sQuery(id+"F0.wireOp",EDGE,"E1.bottom");var subQ6=sQuery(id+"F0.wireOp",EDGE,"E21.filletArc");var subQ7=sQuery(id+"F0.wireOp",EDGE,"E1.top");var subQ8=sQuery(id+"F0.wireOp",EDGE,"E1.left");var subQ9=sQuery(id+"F0.wireOp",EDGE,"E1.right");var subQ10=sQuery(id+"F0.wireOp",EDGE,"E23.filletArc");var subQ11=sQuery(id+"F0.wireOp",EDGE,"E24.filletArc");Q0=makeQuery(id+"F2.boolean.opBoolean","SPLIT",FACE,{"disambiguationData":[TD([makeQuery(id+"F1.opExtrude","SWEPT_FACE",FACE,{"disambiguationData":[OSD([subQ5])]})])],"derivedFrom":makeQuery(id+"F1.opExtrude","CAP_FACE",FACE,{"disambiguationData":[OSD([subQ5,subQ7,subQ8,subQ9,subQ4,subQ3,subQ2,subQ1,subQ6,subQ0,subQ10,subQ11])],"isStart":true})});}
            var sketch = newSketch(context, id + "F16", { "sketchPlane" : qUnion([Q0])});
            skLineSegment(sketch, "E79", {"start": v(0, 90) * mm, "end": v(0, 120) * mm, "construction": true});
            skLineSegment(sketch, "E80", {"start": v(-33, 90) * mm, "end": v(-15, 108) * mm});
            skLineSegment(sketch, "E81", {"start": v(-15, 108) * mm, "end": v(-15, 120) * mm});
            skLineSegment(sketch, "E82", {"start": v(33, 90) * mm, "end": v(15, 108) * mm});
            skLineSegment(sketch, "E83", {"start": v(15, 108) * mm, "end": v(15, 120) * mm});
            skCircle(sketch, "E84", {"center": v(0, 120) * mm, "radius": 6 * mm});
            skArc(sketch, "E85", {"start": v(15, 120) * mm, "mid": v(0, 135) * mm, "end": v(-15, 120) * mm});
            skLineSegment(sketch, "E86", {"start": v(-80, 0) * mm, "end": v(80, 0) * mm, "construction": true});
            skLineSegment(sketch, "E87.MirrorCS", {"start": v(15, -108) * mm, "end": v(15, -120) * mm});
            skLineSegment(sketch, "E88.MirrorCS", {"start": v(33, -90) * mm, "end": v(15, -108) * mm});
            skCircle(sketch, "E89.MirrorC", {"center": v(0, -120) * mm, "radius": 6 * mm});
            skArc(sketch, "E90.MirrorCS", {"start": v(15, -120) * mm, "mid": v(0, -135) * mm, "end": v(-15, -120) * mm});
            skLineSegment(sketch, "E91.MirrorCS", {"start": v(-15, -108) * mm, "end": v(-15, -120) * mm});
            skLineSegment(sketch, "E92.MirrorCS", {"start": v(0, -90) * mm, "end": v(0, -120) * mm, "construction": true});
            skLineSegment(sketch, "E93.MirrorCS", {"start": v(-33, -90) * mm, "end": v(-15, -108) * mm});
            skSolve(sketch);
        }
        {
            var Q0;
            {var subQ1=sQuery(id+"F16.wireOp",EDGE,"E80");Q0=makeQuery(id+"F16.imprint","IMPRINT",FACE,{"disambiguationData":[TD([[makeQuery(id+"F16.imprint","IMPRINT",EDGE,{"derivedFrom":subQ1}),-1.0]])]});}
            var Q1;
            Q1=makeQuery(id+"F16.imprint","IMPRINT",FACE,{"disambiguationData":[TD([[makeQuery(id+"F16.imprint","IMPRINT",EDGE,{"derivedFrom":sQuery(id+"F16.wireOp",EDGE,"E87.MirrorCS")}),-1.0]])]});
            var Q2;
            Q2=makeQuery(id+"F16.imprint","IMPRINT",FACE,{"disambiguationData":[TD([[makeQuery(id+"F16.imprint","IMPRINT",EDGE,{"derivedFrom":makeQuery(id+"F1.opExtrude","CAP_EDGE",EDGE,{"disambiguationData":[OSD([sQuery(id+"F0.wireOp",EDGE,"E1.left")])],"isStart":true})}),-1.0]])]});
            var Q3;
            Q3=makeQuery(id+"F2.opExtrude","CAP_FACE",FACE,{"disambiguationData":[OSD([sQuery(id+"F0.wireOp",EDGE,"E12"),sQuery(id+"F0.wireOp",EDGE,"E13"),sQuery(id+"F0.wireOp",EDGE,"E14"),sQuery(id+"F0.wireOp",EDGE,"E15"),sQuery(id+"F0.wireOp",EDGE,"E17.filletArc"),sQuery(id+"F0.wireOp",EDGE,"E18.filletArc"),sQuery(id+"F0.wireOp",EDGE,"E19.filletArc"),sQuery(id+"F0.wireOp",EDGE,"E20.filletArc"),sQuery(id+"F0.wireOp",EDGE,"E25.0"),sQuery(id+"F0.wireOp",EDGE,"E25.1"),sQuery(id+"F0.wireOp",EDGE,"E25.2"),sQuery(id+"F0.wireOp",EDGE,"E25.3"),sQuery(id+"F0.wireOp",EDGE,"E25.4"),sQuery(id+"F0.wireOp",EDGE,"E25.5"),sQuery(id+"F0.wireOp",EDGE,"E25.6"),sQuery(id+"F0.wireOp",EDGE,"E25.7")])],"isStart":false});
            extrude(context, id + "F17", {"entities" : qUnion([Q0, Q1, Q2]), "endBound" : BoundingType.UP_TO_SURFACE, "endBoundEntityFace" : qUnion([Q3]), "depth" : 25 * mm});
        }
    });
